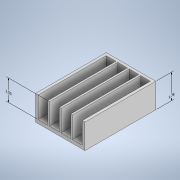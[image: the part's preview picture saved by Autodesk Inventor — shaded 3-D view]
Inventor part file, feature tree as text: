
AUTODESK INVENTOR PART (.ipt)
format: ipt  version: 2021.2 (Build 252289000, 289)  size: 176,640 bytes
history: native  units: in
note: dims shown in document units (in); Inventor stores cm internally (conversion verified against a paired STEP export)
features: other x4, extrude x4, sketch x4, hole x1
ambient origin geometry x8: Origin, YZ Plane, XZ Plane, XY Plane, X Axis, Y Axis, Z Axis, Center Point
bodies: Solid1 (feature_tree)
feature tree (13):
  other  "Annotations"
  extrude  "Extrusion1"  Depth=3.5in
  extrude  "Extrusion2"  Depth=0.1875in
  extrude  "Extrusion3"  Depth=0.1875in
  extrude  "Extrusion4"  Depth=1.5in
  hole  "Hole1"  [1 undecoded]
  sketch  "Sketch2"  dims[d0=5.0in d1=3.5in]
  sketch  "Sketch4"  dims[d2=0.25in d3=0.0in d4=0.1875in]
  sketch  "Sketch6"  dims[d5=1.5in d6=0.0in d7=0.1875in]
  sketch  "Sketch7"  dims[d8=0.1875in d9=1.5in d10=0.0in d11=0.125in d12=0.125in d13=0.125in d14=0.6875in d15=0.6875in d16=0.6875in d17=0.6875in d18=0.3438in d19=1.5in d20=0.0in d21=0.15in d22=0.75in d23=0.279in d24=0.25in d25=0.5635in d26=1.0in d27=0.8108in d28=0.0718in d29=0.1553in d30=0.6875in d31=0.2658in d32=1.75in d33=0.2063in d34=1.5in]
  other  "Linear Dimension 1"
  other  "Linear Dimension 2"
  other  "Linear Dimension 3"
note: 1 required parameter value undecoded (feature->parameter linkage not recoverable at this tier; creation-order binding heuristic only, values carry confidence <= 0.55)
